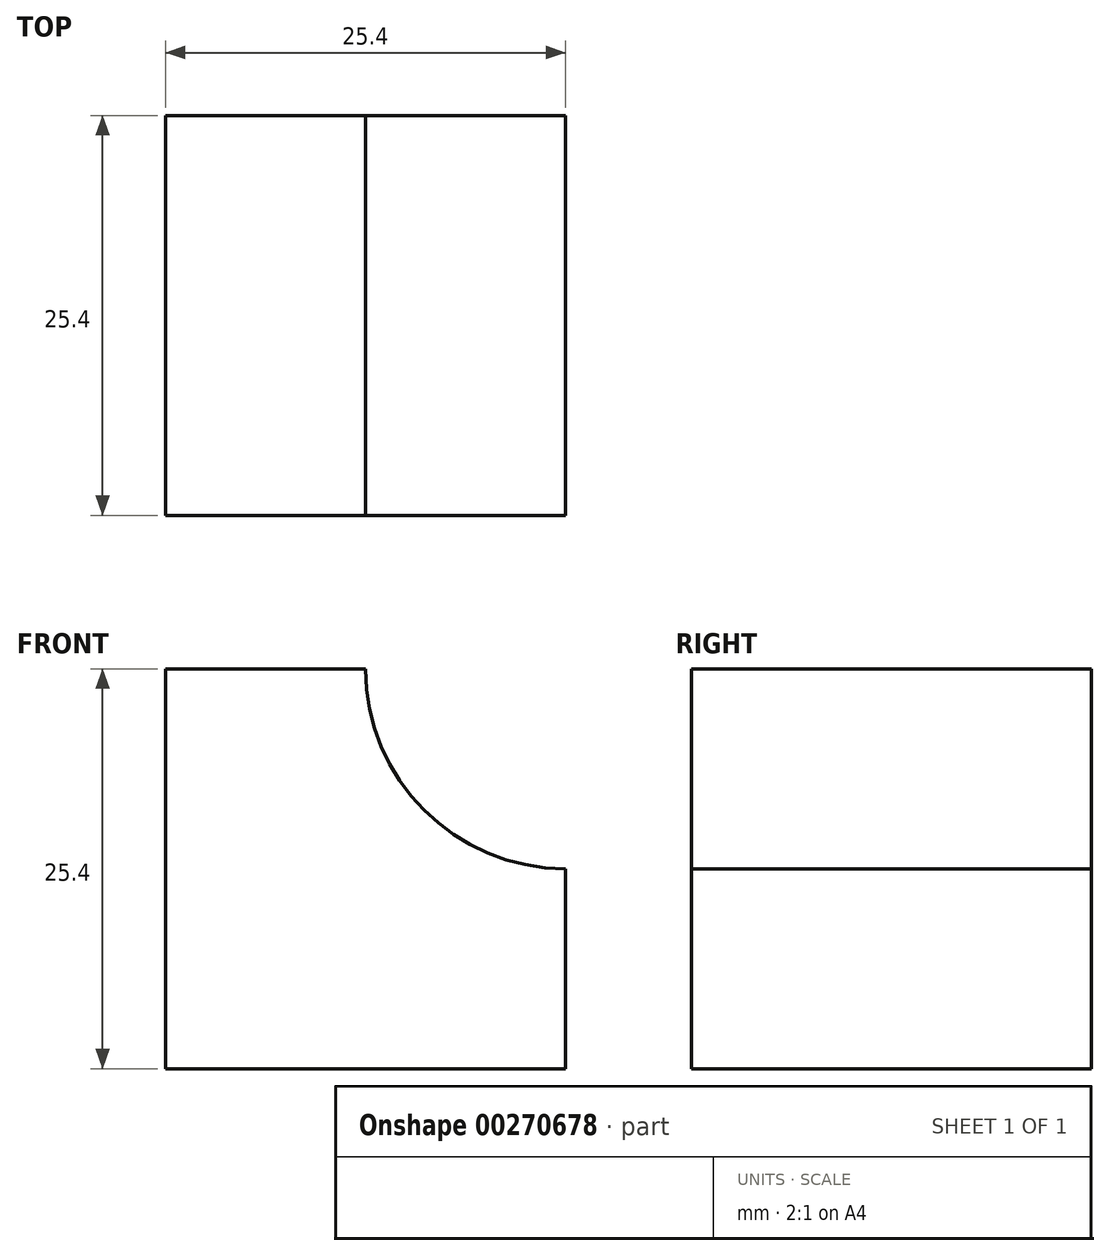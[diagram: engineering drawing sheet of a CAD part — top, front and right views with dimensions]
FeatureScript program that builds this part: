
annotation { "Feature Type Name" : "Feature", "Feature Type Description" : "" }
export const myFeature = defineFeature(function(context is Context, id is Id, definition is map)
    precondition{}
    {
        {
            var Q0;
            Q0=qCreatedBy(makeId("Front.planeOp"),FACE);
            var sketch = newSketch(context, id + "F0", { "sketchPlane" : qUnion([Q0])});
            skLineSegment(sketch, "E0.bottom", {"start": v(0, 0) * mm, "end": v(-25.4, 0) * mm});
            skLineSegment(sketch, "E0.top", {"start": v(0, 25.4) * mm, "end": v(-25.4, 25.4) * mm});
            skLineSegment(sketch, "E0.left", {"start": v(0, 0) * mm, "end": v(0, 25.4) * mm});
            skLineSegment(sketch, "E0.right", {"start": v(-25.4, 0) * mm, "end": v(-25.4, 25.4) * mm});
            skSolve(sketch);
        }
        {
            var Q0;
            Q0=makeQuery(id+"F0.imprint","IMPRINT",FACE,{"disambiguationData":[TD([[makeQuery(id+"F0.imprint","IMPRINT",EDGE,{"derivedFrom":sQuery(id+"F0.wireOp",EDGE,"E0.bottom")}),-1.0]])]});
            extrude(context, id + "F1", {"entities" : qUnion([Q0]), "depth" : 25.4 * mm});
        }
        {
            var Q0;
            Q0=makeQuery(id+"F1.opExtrude","CAP_FACE",FACE,{"disambiguationData":[OSD([sQuery(id+"F0.wireOp",EDGE,"E0.bottom"),sQuery(id+"F0.wireOp",EDGE,"E0.top"),sQuery(id+"F0.wireOp",EDGE,"E0.left"),sQuery(id+"F0.wireOp",EDGE,"E0.right")])],"isStart":false});
            var sketch = newSketch(context, id + "F2", { "sketchPlane" : qUnion([Q0])});
            skArc(sketch, "E1", {"start": v(-12.7, 25.4) * mm, "mid": v(-8.98, 16.42) * mm, "end": v(0, 12.7) * mm});
            skSolve(sketch);
        }
        {
            var Q0;
            {var subQ0=sQuery(id+"F2.wireOp",EDGE,"E1");Q0=makeQuery(id+"F2.imprint","IMPRINT",FACE,{"disambiguationData":[TD([[makeQuery(id+"F2.imprint","IMPRINT",EDGE,{"derivedFrom":subQ0}),1.0]])]});}
            extrude(context, id + "F3", {"entities" : qUnion([Q0]), "operationType" : NewBodyOperationType.REMOVE, "oppositeDirection" : true, "depth" : 25.4 * mm});
        }
    });
